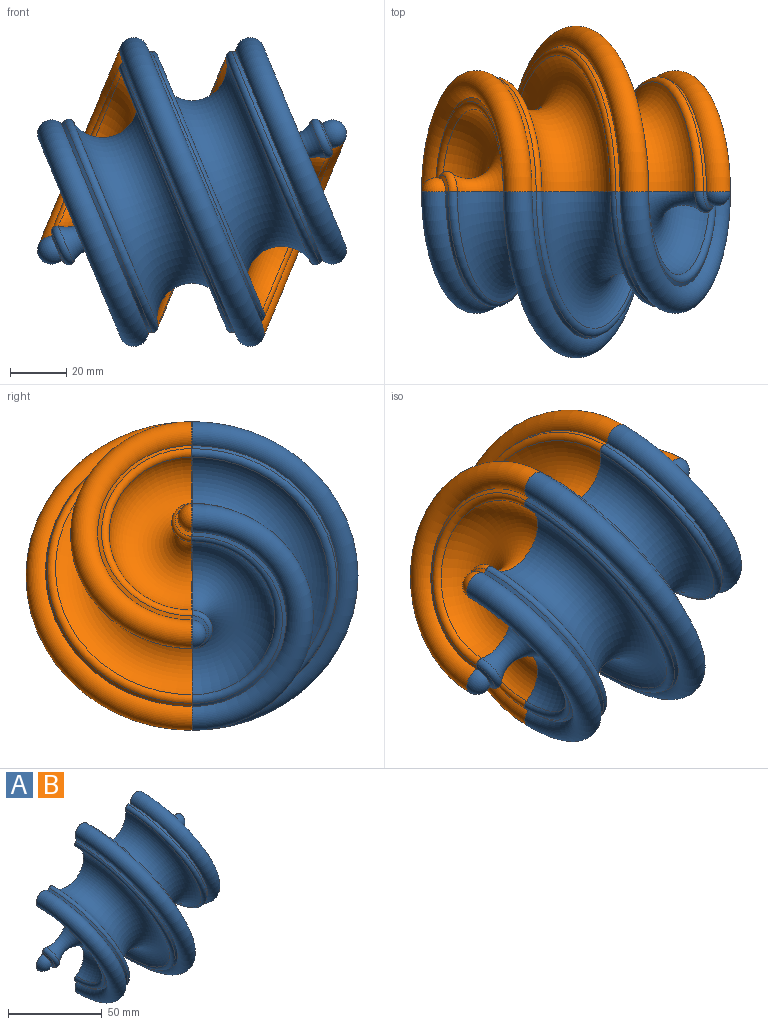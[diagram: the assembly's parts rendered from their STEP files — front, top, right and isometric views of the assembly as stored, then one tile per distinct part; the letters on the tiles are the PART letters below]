
ASSEMBLY  parts=2 mates=1
PART A: 26 faces, bbox 111x64x118.2 mm
  f0: sphere r=5mm, area 108.6mm2, adj f1,f17
  f1: cone r=4.62mm half-angle=67.5deg, axis (-0.92,0,-0.38), area 25.5mm2, adj f0,f17,f18
  f2: torus R=17.22mm, axis (-0.92,0,-0.38), area 2038.8mm2, adj f17,f18,f19
  f3: cone r=29.72mm half-angle=67.5deg, axis (-0.92,0,-0.38), area 157.8mm2, adj f4,f17,f19
  f4: torus R=38.27mm, axis (-0.92,0,-0.38), area 2463.2mm2, adj f3,f5,f17
  f5: cone r=40.18mm half-angle=22.5deg, axis (-0.92,0,-0.38), area 193.8mm2, adj f4,f17,f20
  f6: torus R=41.57mm, axis (-0.92,0,-0.38), area 4922.2mm2, adj f17,f20,f21
  f7: cone r=50.58mm half-angle=22.5deg, axis (-0.92,0,-0.38), area 248.6mm2, adj f8,f17,f21
  f8: torus R=54.12mm, axis (-0.92,0,-0.38), area 3483.5mm2, adj f7,f9,f17
  f9: cone r=52.21mm half-angle=22.5deg, axis (0.92,0,0.38), area 248.6mm2, adj f8,f17,f22
  f10: torus R=41.57mm, axis (-0.92,0,-0.38), area 4922.2mm2, adj f17,f22,f23
  f11: cone r=41.81mm half-angle=22.5deg, axis (0.92,0,0.38), area 193.8mm2, adj f12,f17,f23
  f12: torus R=38.27mm, axis (-0.92,0,-0.38), area 2463.2mm2, adj f11,f13,f17
  f13: cone r=33.65mm half-angle=67.5deg, axis (0.92,0,0.38), area 157.8mm2, adj f12,f17,f24
  f14: torus R=17.22mm, axis (-0.92,0,-0.38), area 2038.8mm2, adj f17,f24,f25
  f15: cone r=8.55mm half-angle=67.5deg, axis (0.92,0,0.38), area 25.5mm2, adj f16,f17,f25
  f16: sphere r=5mm, area 108.6mm2, adj f15,f17
  f17: plane 110x110mm, normal (0,1,0), area 5715.5mm2, adj f0,f1,f2,f3,f4,f5,f6,f7
  f18: torus R=5.26mm, axis (0.92,0,0.38), area 77.5mm2, adj f1,f2,f17
  f19: torus R=31.48mm, axis (0.92,0,0.38), area 342.6mm2, adj f2,f3,f17
  f20: torus R=38.92mm, axis (0.92,0,0.38), area 452.2mm2, adj f5,f6,f17
  f21: torus R=49.78mm, axis (0.92,0,0.38), area 562mm2, adj f6,f7,f17
  f22: torus R=49.78mm, axis (0.92,0,0.38), area 562mm2, adj f9,f10,f17
  f23: torus R=38.92mm, axis (0.92,0,0.38), area 452.2mm2, adj f10,f11,f17
  f24: torus R=31.48mm, axis (0.92,0,0.38), area 342.6mm2, adj f13,f14,f17
  f25: torus R=5.26mm, axis (0.92,0,0.38), area 77.5mm2, adj f14,f15,f17
PART B: same geometry as A
PLACE A at identity fixed
PLACE B rot(axis=(1,0,0),180deg) t=(0,0,0)mm
MATE fastened B.f17 <-> A.f17  axis (0,-1,0) through (0,0,0)mm
